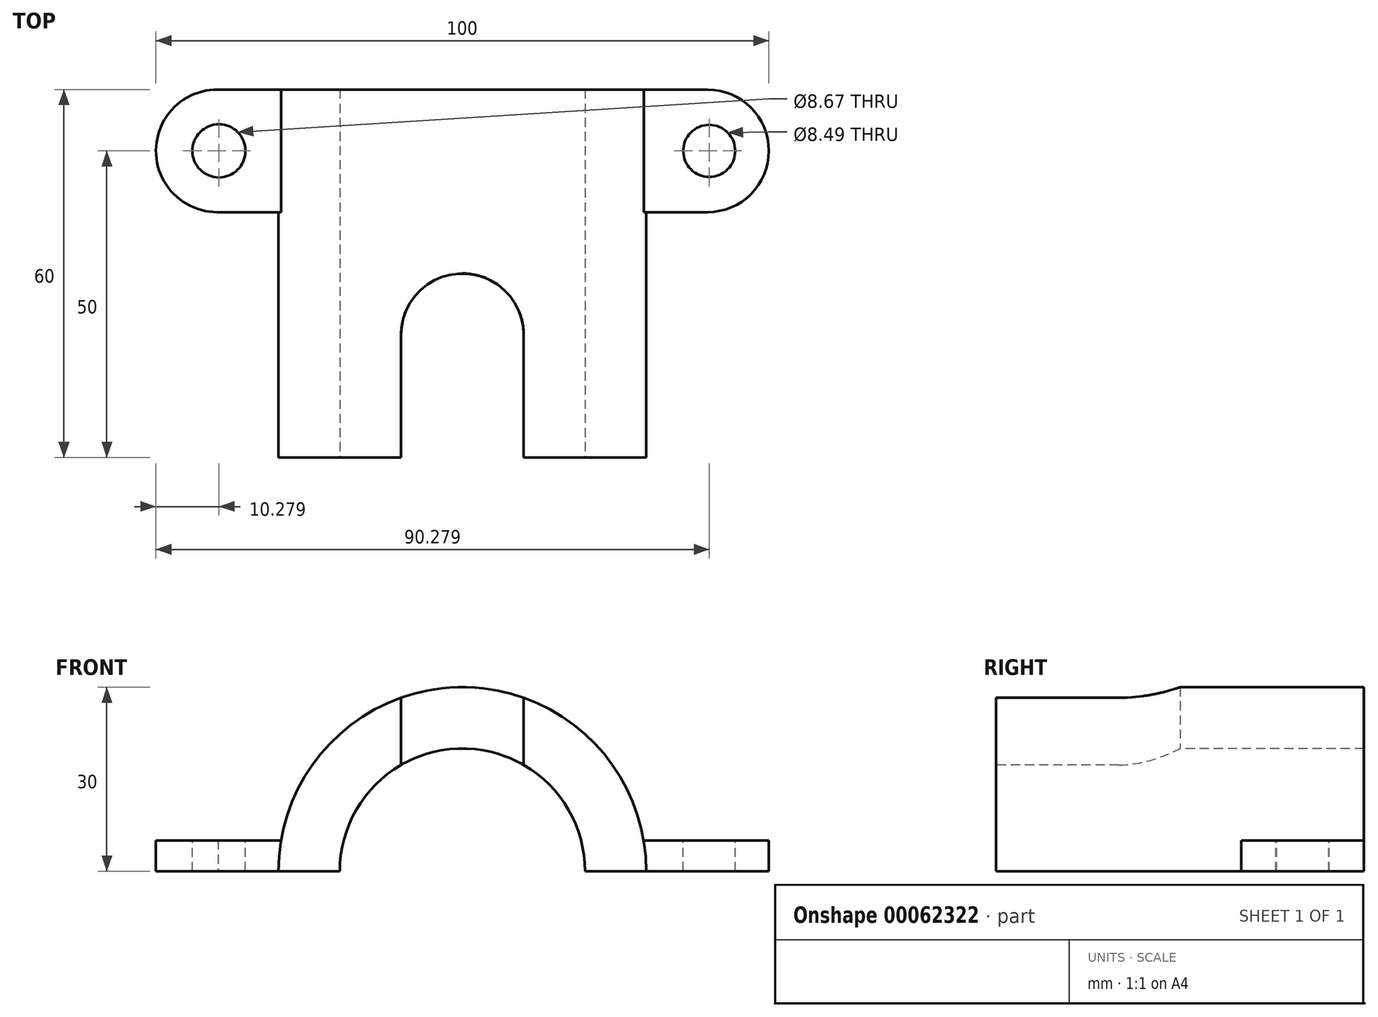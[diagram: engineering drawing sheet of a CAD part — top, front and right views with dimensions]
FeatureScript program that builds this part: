
annotation { "Feature Type Name" : "Feature", "Feature Type Description" : "" }
export const myFeature = defineFeature(function(context is Context, id is Id, definition is map)
    precondition{}
    {
        {
            var Q0;
            Q0=qCreatedBy(makeId("Front.planeOp"),FACE);
            var sketch = newSketch(context, id + "F0", { "sketchPlane" : qUnion([Q0])});
            skArc(sketch, "E0", {"start": v(30, 0) * mm, "mid": v(0, 30) * mm, "end": v(-30, 0) * mm});
            skArc(sketch, "E1", {"start": v(20, 0) * mm, "mid": v(0, 20) * mm, "end": v(-20, 0) * mm});
            skLineSegment(sketch, "E2", {"start": v(20, 0) * mm, "end": v(30, 0) * mm});
            skLineSegment(sketch, "E3", {"start": v(-20, 0) * mm, "end": v(-30, 0) * mm});
            skSolve(sketch);
        }
        {
            var Q0;
            Q0 = qSketchRegion(id + "F0", true);
            extrude(context, id + "F1", {"entities" : qUnion([Q0]), "oppositeDirection" : true, "depth" : 60 * mm});
        }
        {
            var Q0;
            Q0=qCreatedBy(makeId("Top.planeOp"),FACE);
            var sketch = newSketch(context, id + "F2", { "sketchPlane" : qUnion([Q0])});
            skArc(sketch, "E4", {"start": v(-39.87, 60) * mm, "mid": v(-50, 50.07) * mm, "end": v(-40, 40) * mm});
            skArc(sketch, "E5", {"start": v(40, 40) * mm, "mid": v(50, 50) * mm, "end": v(40, 60) * mm});
            skLineSegment(sketch, "E6", {"start": v(-26, 60) * mm, "end": v(-26, 40) * mm});
            skLineSegment(sketch, "E7", {"start": v(26, 60) * mm, "end": v(26, 40) * mm});
            skPoint(sketch, "E8.endSnap0", {"position": v(26, 50.94) * mm});
            skLineSegment(sketch, "E9.0", {"start": v(-40, 40) * mm, "end": v(-26, 40) * mm});
            skLineSegment(sketch, "E10", {"start": v(-39.87, 60) * mm, "end": v(-26, 60) * mm});
            skLineSegment(sketch, "E11", {"start": v(40, 60) * mm, "end": v(26, 60) * mm});
            skLineSegment(sketch, "E12", {"start": v(40, 40) * mm, "end": v(26, 40) * mm});
            skPoint(sketch, "E13.orphan", {"position": v(26, 64.7) * mm});
            skPoint(sketch, "E14.orphan", {"position": v(26, 37.18) * mm});
            skPoint(sketch, "E8.end.orphan", {"position": v(26, 50) * mm});
            skLineSegment(sketch, "E15", {"start": v(-39.87, 60) * mm, "end": v(-39.87, 60) * mm});
            skSolve(sketch);
        }
        {
            var Q0;
            Q0=makeQuery(id+"F2.imprint","IMPRINT",FACE,{"disambiguationData":[TD([[makeQuery(id+"F2.imprint","IMPRINT",EDGE,{"derivedFrom":sQuery(id+"F2.wireOp",EDGE,"E5")}),1.0]])]});
            var Q1;
            Q1=makeQuery(id+"F2.imprint","IMPRINT",FACE,{"disambiguationData":[TD([[makeQuery(id+"F2.imprint","IMPRINT",EDGE,{"derivedFrom":sQuery(id+"F2.wireOp",EDGE,"E4")}),1.0]])]});
            extrude(context, id + "F3", {"entities" : qUnion([Q0, Q1]), "operationType" : NewBodyOperationType.ADD, "depth" : 5 * mm});
        }
        {
            var Q0;
            Q0=makeQuery(id+"F3.opExtrude","CAP_FACE",FACE,{"disambiguationData":[OSD([sQuery(id+"F2.wireOp",EDGE,"E5"),sQuery(id+"F2.wireOp",EDGE,"E7"),sQuery(id+"F2.wireOp",EDGE,"E11"),sQuery(id+"F2.wireOp",EDGE,"E12")])],"isStart":false});
            var sketch = newSketch(context, id + "F4", { "sketchPlane" : qUnion([Q0])});
            skCircle(sketch, "E16", {"center": v(-39.72, 50) * mm, "radius": 4.34 * mm});
            skCircle(sketch, "E17", {"center": v(40.28, 50) * mm, "radius": 4.24 * mm});
            skSolve(sketch);
        }
        {
            var Q0;
            Q0=makeQuery(id+"F4.imprint","IMPRINT",FACE,{"disambiguationData":[TD([[makeQuery(id+"F4.imprint","IMPRINT",EDGE,{"derivedFrom":sQuery(id+"F4.wireOp",EDGE,"E17")}),1.0]])]});
            var Q1;
            Q1=makeQuery(id+"F4.imprint","IMPRINT",FACE,{"disambiguationData":[TD([[makeQuery(id+"F4.imprint","IMPRINT",EDGE,{"derivedFrom":sQuery(id+"F4.wireOp",EDGE,"E16")}),1.0]])]});
            var Q2;
            Q2=sQuery(id+"F4.wireOp",EDGE,"E17");
            var Q3;
            Q3=sQuery(id+"F4.wireOp",EDGE,"E16");
            extrude(context, id + "F5", {"entities" : qUnion([Q0, Q1]), "operationType" : NewBodyOperationType.REMOVE, "surfaceEntities" : qUnion([Q2, Q3]), "oppositeDirection" : true, "depth" : 5 * mm});
        }
        {
            var Q0;
            Q0=qCreatedBy(makeId("Top.planeOp"),FACE);
            var sketch = newSketch(context, id + "F6", { "sketchPlane" : qUnion([Q0])});
            skArc(sketch, "E18", {"start": v(10, 20) * mm, "mid": v(0, 30) * mm, "end": v(-10, 20) * mm});
            skLineSegment(sketch, "E19.0", {"start": v(-10, 0) * mm, "end": v(-10, 20) * mm});
            skLineSegment(sketch, "E20.0", {"start": v(10, 0) * mm, "end": v(10, 20) * mm});
            skLineSegment(sketch, "E21", {"start": v(-10, 0) * mm, "end": v(10, 0) * mm});
            skSolve(sketch);
        }
        {
            var Q0;
            Q0 = qSketchRegion(id + "F6", true);
            extrude(context, id + "F7", {"entities" : qUnion([Q0]), "operationType" : NewBodyOperationType.REMOVE, "depth" : 30 * mm});
        }
    });
